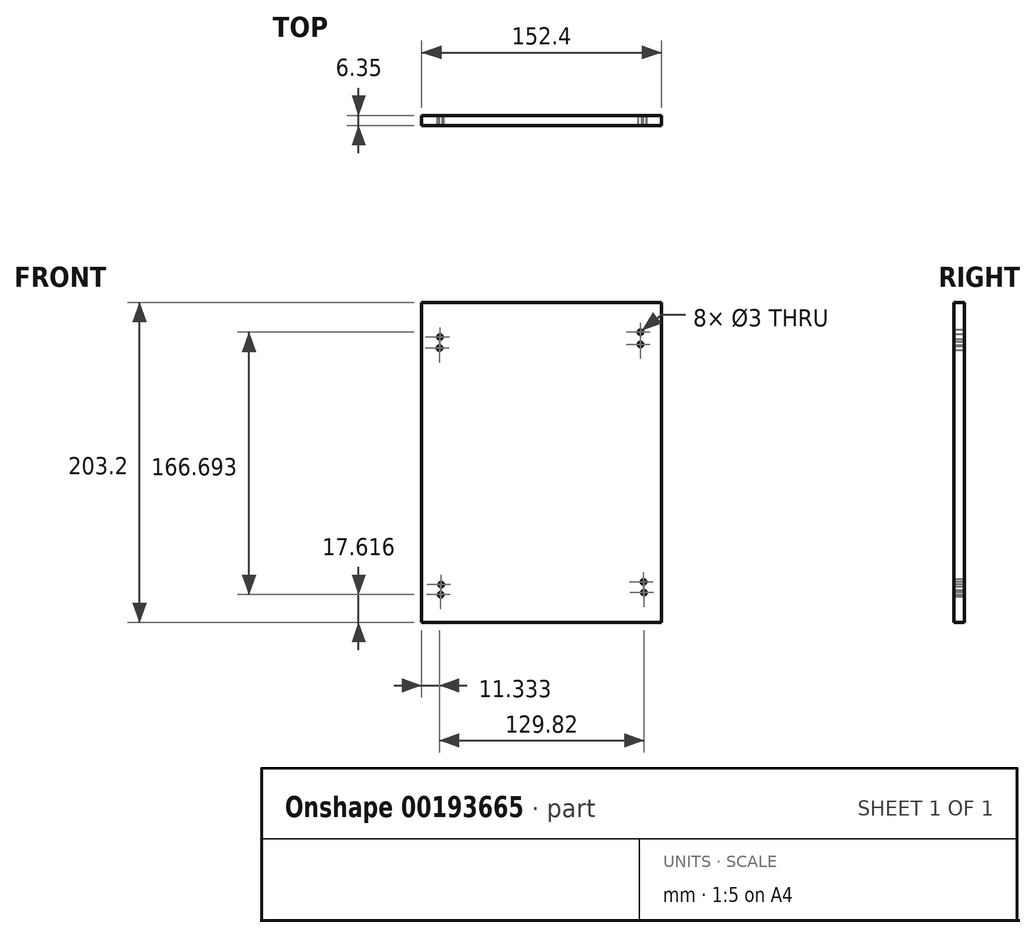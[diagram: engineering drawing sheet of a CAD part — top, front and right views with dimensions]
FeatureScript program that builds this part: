
annotation { "Feature Type Name" : "Feature", "Feature Type Description" : "" }
export const myFeature = defineFeature(function(context is Context, id is Id, definition is map)
    precondition{}
    {
        {
            var Q0;
            Q0=qCreatedBy(makeId("Front.planeOp"),FACE);
            var sketch = newSketch(context, id + "F0", { "sketchPlane" : qUnion([Q0])});
            skLineSegment(sketch, "E0.bottom", {"start": v(76.2, 101.6) * mm, "end": v(-76.2, 101.6) * mm});
            skLineSegment(sketch, "E0.top", {"start": v(76.2, -101.6) * mm, "end": v(-76.2, -101.6) * mm});
            skLineSegment(sketch, "E0.left", {"start": v(76.2, 101.6) * mm, "end": v(76.2, -101.6) * mm});
            skLineSegment(sketch, "E0.right", {"start": v(-76.2, 101.6) * mm, "end": v(-76.2, -101.6) * mm});
            skPoint(sketch, "E0.middle", {"position": v(0, 0) * mm});
            skSolve(sketch);
        }
        {
            var Q0;
            Q0=makeQuery(id+"F0.imprint","IMPRINT",FACE,{"disambiguationData":[TD([[makeQuery(id+"F0.imprint","IMPRINT",EDGE,{"derivedFrom":sQuery(id+"F0.wireOp",EDGE,"E0.bottom")}),1.0]])]});
            extrude(context, id + "F1", {"entities" : qUnion([Q0]), "depth" : 6.35 * mm});
        }
        {
            var Q0;
            Q0=makeQuery(id+"F1.opExtrude","CAP_FACE",FACE,{"disambiguationData":[OSD([sQuery(id+"F0.wireOp",EDGE,"E0.bottom"),sQuery(id+"F0.wireOp",EDGE,"E0.top"),sQuery(id+"F0.wireOp",EDGE,"E0.left"),sQuery(id+"F0.wireOp",EDGE,"E0.right")])],"isStart":false});
            var sketch = newSketch(context, id + "F2", { "sketchPlane" : qUnion([Q0])});
            skLineSegment(sketch, "E1", {"start": v(-64.77, 101.6) * mm, "end": v(-64.77, 79.59) * mm});
            skLineSegment(sketch, "E2", {"start": v(-64.77, 79.59) * mm, "end": v(-64.77, 73.24) * mm});
            skSolve(sketch);
        }
        {
            var Q0;
            Q0=makeQuery(id+"F2.imprint","IMPRINT",FACE,{"disambiguationData":[TD([[makeQuery(id+"F2.imprint","IMPRINT",EDGE,{"derivedFrom":makeQuery(id+"F1.opExtrude","CAP_EDGE",EDGE,{"disambiguationData":[OSD([sQuery(id+"F0.wireOp",EDGE,"E0.top")])],"isStart":false})}),-1.0]])]});
            var sketch = newSketch(context, id + "F3", { "sketchPlane" : qUnion([Q0])});
            skCircle(sketch, "E3", {"center": v(-64.64, 79.63) * mm, "radius": 1.5 * mm});
            skCircle(sketch, "E4", {"center": v(-64.57, 72.93) * mm, "radius": 0.15 * mm});
            skSolve(sketch);
        }
        {
            var Q0;
            Q0=makeQuery(id+"F2.imprint","IMPRINT",FACE,{"disambiguationData":[TD([[makeQuery(id+"F2.imprint","IMPRINT",EDGE,{"derivedFrom":makeQuery(id+"F1.opExtrude","CAP_EDGE",EDGE,{"disambiguationData":[OSD([sQuery(id+"F0.wireOp",EDGE,"E0.top")])],"isStart":false})}),-1.0]])]});
            var sketch = newSketch(context, id + "F4", { "sketchPlane" : qUnion([Q0])});
            skCircle(sketch, "E5", {"center": v(-64.87, 72.63) * mm, "radius": 1.5 * mm});
            skSolve(sketch);
        }
        {
            var Q0;
            Q0=sQuery(id+"F3.wireOp",EDGE,"E3");
            extrude(context, id + "F5", {"bodyType" : ToolBodyType.SURFACE, "surfaceEntities" : qUnion([Q0]), "oppositeDirection" : true, "depth" : 6.35 * mm});
        }
        {
            var Q0;
            Q0 = qSketchRegion(id + "F3", true);
            extrude(context, id + "F6", {"entities" : qUnion([Q0]), "operationType" : NewBodyOperationType.REMOVE, "oppositeDirection" : true, "depth" : 6.35 * mm});
        }
        {
            var Q0;
            Q0 = qSketchRegion(id + "F4", true);
            var Q1;
            Q1=sQuery(id+"F4.wireOp",EDGE,"E5");
            extrude(context, id + "F7", {"entities" : qUnion([Q0]), "operationType" : NewBodyOperationType.REMOVE, "surfaceEntities" : qUnion([Q1]), "oppositeDirection" : true, "depth" : 6.35 * mm});
        }
        {
            var Q0;
            Q0=makeQuery(id+"F2.imprint","IMPRINT",FACE,{"disambiguationData":[TD([[makeQuery(id+"F2.imprint","IMPRINT",EDGE,{"derivedFrom":makeQuery(id+"F1.opExtrude","CAP_EDGE",EDGE,{"disambiguationData":[OSD([sQuery(id+"F0.wireOp",EDGE,"E0.top")])],"isStart":false})}),-1.0]])]});
            var sketch = newSketch(context, id + "F8", { "sketchPlane" : qUnion([Q0])});
            skCircle(sketch, "E6", {"center": v(62.74, 82.7) * mm, "radius": 1.5 * mm});
            skCircle(sketch, "E7", {"center": v(62.8, 75.01) * mm, "radius": 1.5 * mm});
            skSolve(sketch);
        }
        {
            var Q0;
            Q0 = qSketchRegion(id + "F8", true);
            extrude(context, id + "F9", {"entities" : qUnion([Q0]), "operationType" : NewBodyOperationType.REMOVE, "oppositeDirection" : true, "depth" : 6.35 * mm});
        }
        {
            var Q0;
            Q0=makeQuery(id+"F2.imprint","IMPRINT",FACE,{"disambiguationData":[TD([[makeQuery(id+"F2.imprint","IMPRINT",EDGE,{"derivedFrom":makeQuery(id+"F1.opExtrude","CAP_EDGE",EDGE,{"disambiguationData":[OSD([sQuery(id+"F0.wireOp",EDGE,"E0.top")])],"isStart":false})}),-1.0]])]});
            var sketch = newSketch(context, id + "F10", { "sketchPlane" : qUnion([Q0])});
            skCircle(sketch, "E8", {"center": v(-63.82, -77.54) * mm, "radius": 1.5 * mm});
            skCircle(sketch, "E9", {"center": v(-64.12, -83.98) * mm, "radius": 1.5 * mm});
            skSolve(sketch);
        }
        {
            var Q0;
            Q0 = qSketchRegion(id + "F10", true);
            extrude(context, id + "F11", {"entities" : qUnion([Q0]), "operationType" : NewBodyOperationType.REMOVE, "oppositeDirection" : true, "depth" : 6.35 * mm});
        }
        {
            var Q0;
            Q0=makeQuery(id+"F2.imprint","IMPRINT",FACE,{"disambiguationData":[TD([[makeQuery(id+"F2.imprint","IMPRINT",EDGE,{"derivedFrom":makeQuery(id+"F1.opExtrude","CAP_EDGE",EDGE,{"disambiguationData":[OSD([sQuery(id+"F0.wireOp",EDGE,"E0.top")])],"isStart":false})}),-1.0]])]});
            var sketch = newSketch(context, id + "F12", { "sketchPlane" : qUnion([Q0])});
            skCircle(sketch, "E10", {"center": v(64.74, -75.92) * mm, "radius": 1.5 * mm});
            skCircle(sketch, "E11", {"center": v(64.95, -82.7) * mm, "radius": 1.5 * mm});
            skSolve(sketch);
        }
        {
            var Q0;
            Q0 = qSketchRegion(id + "F12", true);
            extrude(context, id + "F13", {"entities" : qUnion([Q0]), "operationType" : NewBodyOperationType.REMOVE, "oppositeDirection" : true, "depth" : 6.35 * mm});
        }
    });
